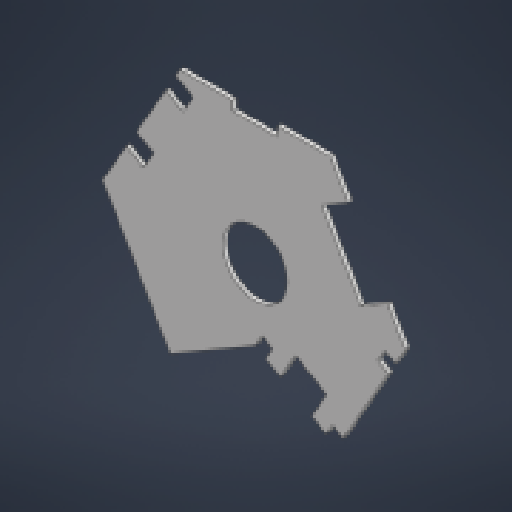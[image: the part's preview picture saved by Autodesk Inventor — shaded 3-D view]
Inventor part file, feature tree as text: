
AUTODESK INVENTOR PART (.ipt)
format: ipt  version: 2023 (Build 270158000, 158)  size: 235,008 bytes
history: native  units: in
note: dims shown in document units (in); Inventor stores cm internally (conversion verified against a paired STEP export)
features: extrude x1, sketch x1
ambient origin geometry x8: Origin, YZ Plane, XZ Plane, XY Plane, X Axis, Y Axis, Z Axis, Center Point
bodies: Solid1 (feature_tree)
feature tree (2):
  extrude  "Extrusion1"  Depth=0.0394in
  sketch  "Sketch1"  dims[d0=2.5394in d1=0.1287in d2=0.0394in d3=0.6299in d4=0.4626in d5=0.1937in d6=0.1969in d7=0.5709in d8=0.1945in d9=0.1969in d10=0.2185in d11=0.2185in d12=0.0909in d13=0.3819in d14=0.3819in d15=0.2992in d16=0.1949in d17=0.1201in d18=0.1339in d19=0.8858in d21=0.1205in d22=0.176in d23=0.176in d24=0.2937in d25=0.1661in d26=0.1339in d27=0.0394in d28=0.0in]
